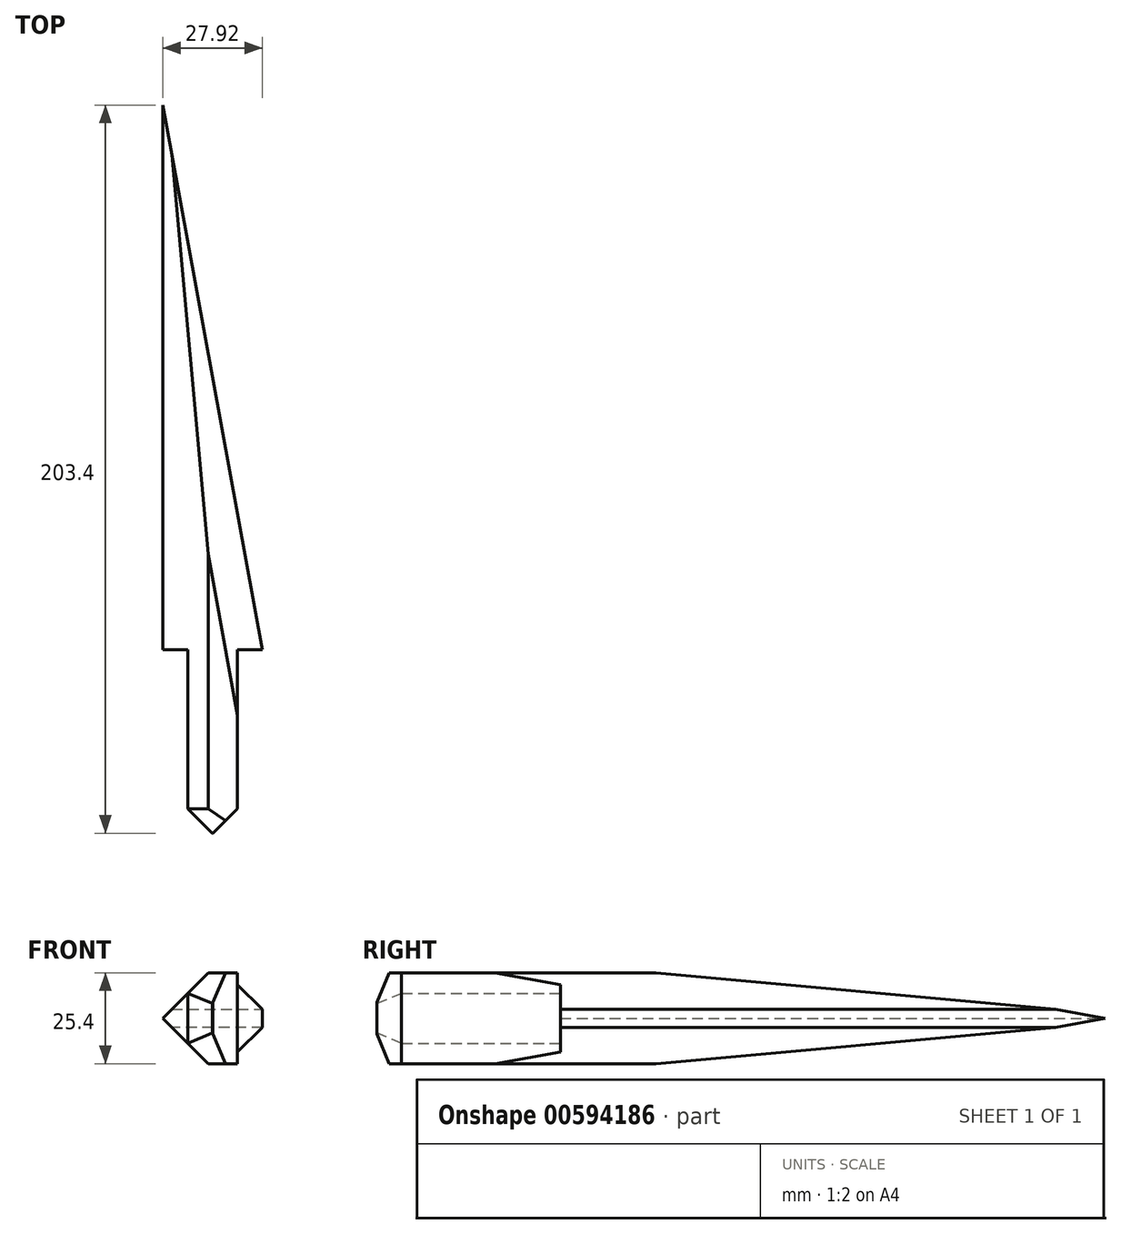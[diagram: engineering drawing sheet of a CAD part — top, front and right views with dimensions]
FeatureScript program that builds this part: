
annotation { "Feature Type Name" : "Feature", "Feature Type Description" : "" }
export const myFeature = defineFeature(function(context is Context, id is Id, definition is map)
    precondition{}
    {
        {
            var Q0;
            Q0=qCreatedBy(makeId("Top.planeOp"),FACE);
            var sketch = newSketch(context, id + "F0", { "sketchPlane" : qUnion([Q0])});
            skLineSegment(sketch, "E0", {"start": v(0, 0) * mm, "end": v(13.96, 0) * mm});
            skLineSegment(sketch, "E1", {"start": v(0, 0) * mm, "end": v(-13.96, 0) * mm});
            skLineSegment(sketch, "E2", {"start": v(-13.96, 0) * mm, "end": v(0, 0) * mm});
            skLineSegment(sketch, "E3", {"start": v(-6.98, 0) * mm, "end": v(0, 0) * mm});
            skLineSegment(sketch, "E4", {"start": v(-13.96, 0) * mm, "end": v(-13.96, 76.09) * mm});
            skLineSegment(sketch, "E5", {"start": v(-13.96, 76.09) * mm, "end": v(-13.96, 0) * mm});
            skLineSegment(sketch, "E6", {"start": v(13.96, 0) * mm, "end": v(0, 76.09) * mm});
            skLineSegment(sketch, "E7", {"start": v(0, 76.09) * mm, "end": v(-11.12, 136.72) * mm});
            skLineSegment(sketch, "E8", {"start": v(-11.12, 136.72) * mm, "end": v(-13.96, 152.17) * mm});
            skLineSegment(sketch, "E9", {"start": v(-13.96, 152.17) * mm, "end": v(-13.96, 76.09) * mm});
            skLineSegment(sketch, "E10", {"start": v(6.98, 0) * mm, "end": v(6.98, -30.66) * mm});
            skLineSegment(sketch, "E11", {"start": v(6.98, -30.66) * mm, "end": v(-4.94, -30.66) * mm});
            skLineSegment(sketch, "E12", {"start": v(-6.98, 0) * mm, "end": v(-6.98, -30.66) * mm});
            skLineSegment(sketch, "E13", {"start": v(-6.98, -30.66) * mm, "end": v(-4.94, -30.66) * mm});
            skSolve(sketch);
        }
        {
            var Q0;
            Q0 = qSketchRegion(id + "F0", true);
            extrude(context, id + "F1", {"entities" : qUnion([Q0]), "depth" : 25.4 * mm, "offsetDistance" : 25.4 * mm});
        }
        {
            var Q0;
            Q0=makeQuery(id+"F1.opExtrude","CAP_EDGE",EDGE,{"disambiguationData":[OSD([sQuery(id+"F0.wireOp",EDGE,"E5"),sQuery(id+"F0.wireOp",EDGE,"E9")])],"isStart":false});
            var Q1;
            Q1=makeQuery(id+"F1.opExtrude","CAP_EDGE",EDGE,{"disambiguationData":[OSD([sQuery(id+"F0.wireOp",EDGE,"E5"),sQuery(id+"F0.wireOp",EDGE,"E9")])],"isStart":true});
            chamfer(context, id + "F2", {"entities" : qUnion([Q0, Q1]), "width" : 12.7 * mm, "tangentPropagation" : true});
        }
        {
            var Q0;
            Q0=makeQuery(id+"F1.opExtrude","CAP_EDGE",EDGE,{"disambiguationData":[OSD([sQuery(id+"F0.wireOp",EDGE,"E6"),sQuery(id+"F0.wireOp",EDGE,"E7"),sQuery(id+"F0.wireOp",EDGE,"E8")])],"isStart":false});
            var Q1;
            Q1=makeQuery(id+"F1.opExtrude","CAP_EDGE",EDGE,{"disambiguationData":[OSD([sQuery(id+"F0.wireOp",EDGE,"E6"),sQuery(id+"F0.wireOp",EDGE,"E7"),sQuery(id+"F0.wireOp",EDGE,"E8")])],"isStart":true});
            chamfer(context, id + "F3", {"entities" : qUnion([Q0, Q1]), "width" : 10.16 * mm, "tangentPropagation" : true});
        }
        {
            var Q0;
            Q0=makeQuery(id+"F1.opExtrude","SWEPT_FACE",FACE,{"disambiguationData":[OSD([sQuery(id+"F0.wireOp",EDGE,"E11"),sQuery(id+"F0.wireOp",EDGE,"E13")])]});
            extrude(context, id + "F4", {"entities" : qUnion([Q0]), "operationType" : NewBodyOperationType.ADD, "depth" : 20.57 * mm, "offsetDistance" : 25.4 * mm});
        }
        {
            var Q0;
            Q0=makeQuery(id+"F4.opExtrude","CAP_FACE",FACE,{"disambiguationData":[OSD([sQuery(id+"F0.wireOp",EDGE,"E11"),sQuery(id+"F0.wireOp",EDGE,"E13")])],"isStart":false});
            chamfer(context, id + "F5", {"entities" : qUnion([Q0]), "width" : 6.86 * mm, "tangentPropagation" : true});
        }
    });
